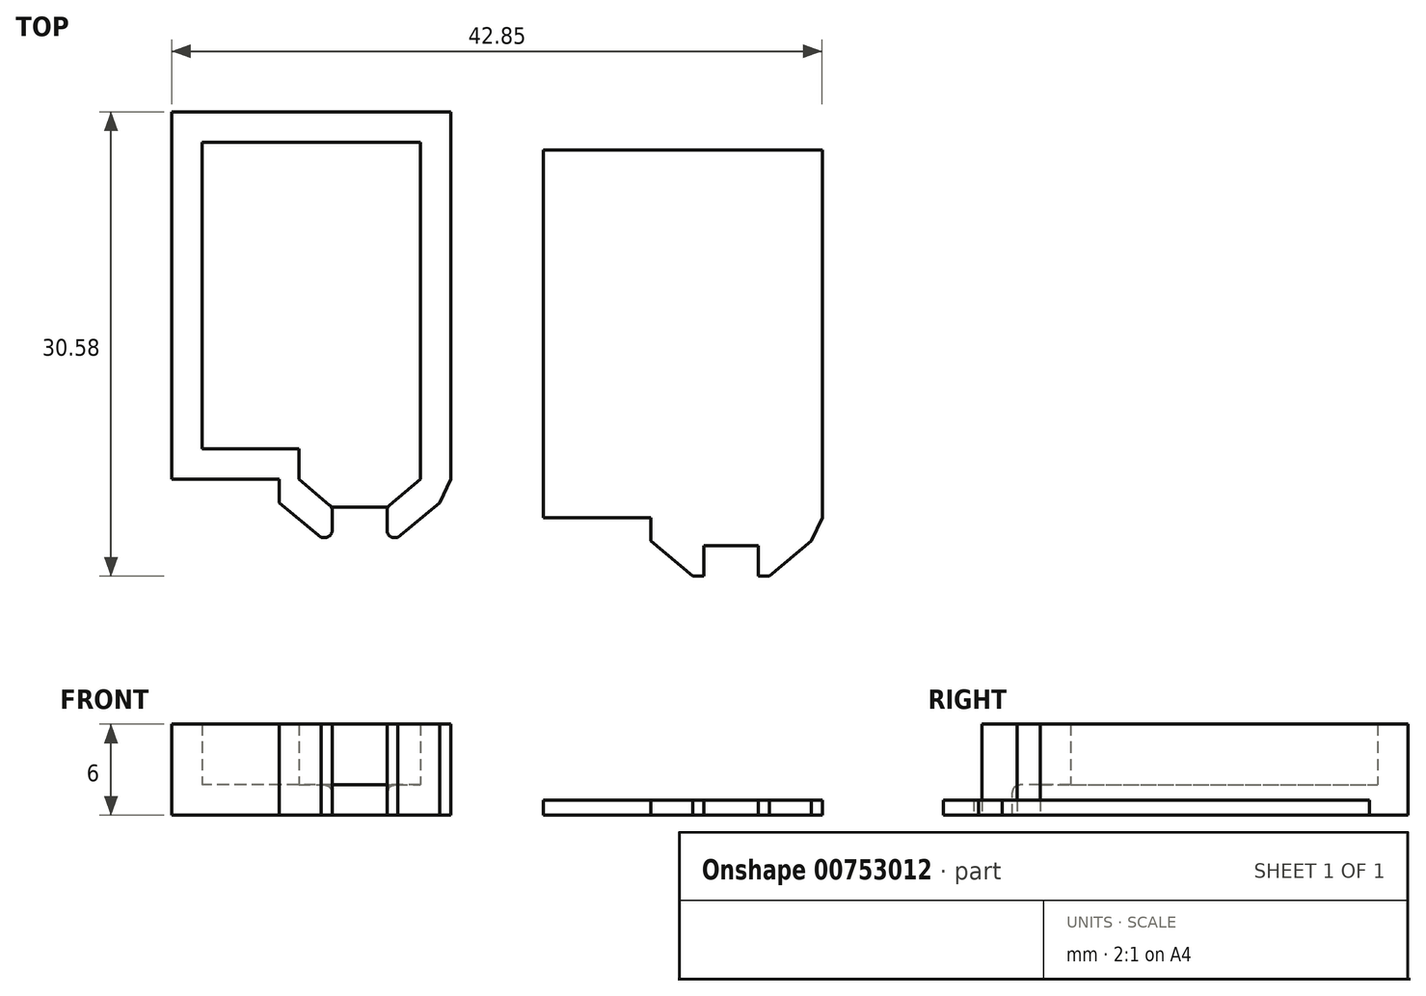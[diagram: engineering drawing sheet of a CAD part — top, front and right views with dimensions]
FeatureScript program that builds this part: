
annotation { "Feature Type Name" : "Feature", "Feature Type Description" : "" }
export const myFeature = defineFeature(function(context is Context, id is Id, definition is map)
    precondition{}
    {
        {
            var Q0;
            Q0=qCreatedBy(makeId("Top.planeOp"),FACE);
            var sketch = newSketch(context, id + "F0", { "sketchPlane" : qUnion([Q0])});
            skLineSegment(sketch, "E0.bottom", {"start": v(7.2, -10.1) * mm, "end": v(-7.19, -10.1) * mm});
            skLineSegment(sketch, "E0.top", {"start": v(7.2, 10.1) * mm, "end": v(-7.19, 10.1) * mm});
            skLineSegment(sketch, "E0.left", {"start": v(7.2, -10.1) * mm, "end": v(7.2, 10.1) * mm});
            skLineSegment(sketch, "E0.right", {"start": v(-7.19, -10.1) * mm, "end": v(-7.19, 10.1) * mm});
            skPoint(sketch, "E0.middle", {"position": v(0, 0) * mm});
            skLineSegment(sketch, "E1.0", {"start": v(9.2, 12.1) * mm, "end": v(-9.19, 12.1) * mm});
            skLineSegment(sketch, "E1.1", {"start": v(9.2, -12.1) * mm, "end": v(9.2, 12.1) * mm});
            skLineSegment(sketch, "E1.2", {"start": v(9.2, -12.1) * mm, "end": v(7.2, -12.1) * mm});
            skLineSegment(sketch, "E1.3", {"start": v(-9.19, -12.1) * mm, "end": v(-9.19, 12.1) * mm});
            skLineSegment(sketch, "E2", {"start": v(7.2, -10.1) * mm, "end": v(7.2, -12.1) * mm});
            skPoint(sketch, "E2.endSnap0", {"position": v(0, -12.1) * mm});
            skLineSegment(sketch, "E3", {"start": v(7.2, -10.1) * mm, "end": v(-0.8, -10.1) * mm, "construction": true});
            skLineSegment(sketch, "E4", {"start": v(-0.8, -10.1) * mm, "end": v(-0.8, -12.1) * mm});
            skLineSegment(sketch, "E5.trimOffspring", {"start": v(-0.8, -12.1) * mm, "end": v(-9.2, -12.1) * mm});
            skLineSegment(sketch, "E6", {"start": v(-0.8, -12.1) * mm, "end": v(7.2, -12.1) * mm});
            skLineSegment(sketch, "E7", {"start": v(-0.8, -12.1) * mm, "end": v(1.4, -13.95) * mm});
            skLineSegment(sketch, "E8", {"start": v(1.4, -13.95) * mm, "end": v(5, -13.95) * mm});
            skLineSegment(sketch, "E9", {"start": v(5, -13.95) * mm, "end": v(7.2, -12.1) * mm});
            skLineSegment(sketch, "E10", {"start": v(-0.8, -12.1) * mm, "end": v(3.2, -12.1) * mm, "construction": true});
            skLineSegment(sketch, "E11", {"start": v(3.2, -12.1) * mm, "end": v(3.2, -19.26) * mm, "construction": true});
            skLineSegment(sketch, "E12.0", {"start": v(5.72, -15.95) * mm, "end": v(8.48, -13.64) * mm});
            skLineSegment(sketch, "E12.1", {"start": v(0.66, -15.95) * mm, "end": v(5.72, -15.95) * mm});
            skLineSegment(sketch, "E12.2", {"start": v(-2.1, -13.64) * mm, "end": v(0.66, -15.95) * mm});
            skLineSegment(sketch, "E13", {"start": v(-2.1, -13.64) * mm, "end": v(-2.1, -12.1) * mm});
            skLineSegment(sketch, "E14", {"start": v(8.48, -13.64) * mm, "end": v(9.2, -12.1) * mm});
            skLineSegment(sketch, "E15", {"start": v(1.4, -13.95) * mm, "end": v(1.4, -15.95) * mm});
            skLineSegment(sketch, "E16", {"start": v(5, -13.95) * mm, "end": v(5, -15.95) * mm});
            skSolve(sketch);
        }
        {
            var Q0;
            Q0=makeQuery(id+"F0.imprint","IMPRINT",FACE,{"disambiguationData":[TD([[makeQuery(id+"F0.imprint","IMPRINT",EDGE,{"derivedFrom":sQuery(id+"F0.wireOp",EDGE,"E0.top")}),1.0]])]});
            extrude(context, id + "F1", {"entities" : qUnion([Q0]), "depth" : 2 * mm, "offsetDistance" : 25 * mm});
        }
        {
            var Q0;
            Q0=makeQuery(id+"F0.imprint","IMPRINT",FACE,{"disambiguationData":[TD([[makeQuery(id+"F0.imprint","IMPRINT",EDGE,{"derivedFrom":sQuery(id+"F0.wireOp",EDGE,"E0.top")}),-1.0]])]});
            extrude(context, id + "F2", {"entities" : qUnion([Q0]), "operationType" : NewBodyOperationType.ADD, "depth" : 5 * mm, "offsetDistance" : 25 * mm});
        }
        {
            var Q0;
            {var subQ0=sQuery(id+"F0.wireOp",EDGE,"E2");Q0=makeQuery(id+"F0.imprint","IMPRINT",FACE,{"disambiguationData":[TD([[makeQuery(id+"F0.imprint","IMPRINT",EDGE,{"derivedFrom":subQ0}),-1.0]])]});}
            extrude(context, id + "F3", {"entities" : qUnion([Q0]), "operationType" : NewBodyOperationType.ADD, "depth" : 2 * mm, "offsetDistance" : 25 * mm});
        }
        {
            var Q0;
            Q0=makeQuery(id+"F0.imprint","IMPRINT",FACE,{"disambiguationData":[TD([[makeQuery(id+"F0.imprint","IMPRINT",EDGE,{"derivedFrom":sQuery(id+"F0.wireOp",EDGE,"E6")}),-1.0]])]});
            extrude(context, id + "F4", {"entities" : qUnion([Q0]), "operationType" : NewBodyOperationType.ADD, "depth" : 2 * mm, "offsetDistance" : 25 * mm});
        }
        {
            var Q0;
            {var subQ3=sQuery(id+"F0.wireOp",EDGE,"E7");Q0=makeQuery(id+"F0.imprint","IMPRINT",FACE,{"disambiguationData":[TD([[makeQuery(id+"F0.imprint","IMPRINT",EDGE,{"derivedFrom":subQ3}),-1.0]])]});}
            var Q1;
            Q1=makeQuery(id+"F0.imprint","IMPRINT",FACE,{"disambiguationData":[TD([[makeQuery(id+"F0.imprint","IMPRINT",EDGE,{"derivedFrom":sQuery(id+"F0.wireOp",EDGE,"E1.2")}),1.0]])]});
            extrude(context, id + "F5", {"entities" : qUnion([Q0, Q1]), "operationType" : NewBodyOperationType.ADD, "depth" : 5 * mm, "offsetDistance" : 25 * mm});
        }
        {
            var Q0;
            Q0=qCreatedBy(makeId("Top.planeOp"),FACE);
            var sketch = newSketch(context, id + "F6", { "sketchPlane" : qUnion([Q0])});
            skLineSegment(sketch, "E17.bottom", {"start": v(31.66, -12.63) * mm, "end": v(17.28, -12.63) * mm});
            skLineSegment(sketch, "E17.top", {"start": v(31.66, 7.58) * mm, "end": v(17.28, 7.58) * mm});
            skLineSegment(sketch, "E17.left", {"start": v(31.66, -12.63) * mm, "end": v(31.66, 7.58) * mm});
            skLineSegment(sketch, "E17.right", {"start": v(17.28, -12.63) * mm, "end": v(17.28, 7.58) * mm});
            skPoint(sketch, "E17.middle", {"position": v(24.47, -2.53) * mm});
            skLineSegment(sketch, "E18.0", {"start": v(33.66, 9.58) * mm, "end": v(15.28, 9.58) * mm});
            skLineSegment(sketch, "E18.1", {"start": v(33.66, -14.63) * mm, "end": v(33.66, 9.58) * mm});
            skLineSegment(sketch, "E18.2", {"start": v(33.66, -14.63) * mm, "end": v(31.66, -14.63) * mm});
            skLineSegment(sketch, "E18.3", {"start": v(15.28, -14.63) * mm, "end": v(15.28, 9.58) * mm});
            skLineSegment(sketch, "E19", {"start": v(31.66, -12.63) * mm, "end": v(31.66, -14.63) * mm});
            skPoint(sketch, "E19.endSnap0", {"position": v(24.47, -14.63) * mm});
            skLineSegment(sketch, "E20", {"start": v(31.66, -12.63) * mm, "end": v(23.66, -12.63) * mm, "construction": true});
            skLineSegment(sketch, "E21", {"start": v(23.66, -12.63) * mm, "end": v(23.66, -14.63) * mm});
            skLineSegment(sketch, "E22.trimOffspring", {"start": v(23.66, -14.63) * mm, "end": v(15.28, -14.63) * mm});
            skLineSegment(sketch, "E23", {"start": v(23.66, -14.63) * mm, "end": v(31.66, -14.63) * mm});
            skLineSegment(sketch, "E24", {"start": v(23.66, -14.63) * mm, "end": v(25.86, -16.48) * mm});
            skLineSegment(sketch, "E25", {"start": v(25.86, -16.48) * mm, "end": v(29.46, -16.48) * mm});
            skLineSegment(sketch, "E26", {"start": v(29.46, -16.48) * mm, "end": v(31.66, -14.63) * mm});
            skLineSegment(sketch, "E27", {"start": v(23.66, -14.63) * mm, "end": v(27.66, -14.63) * mm, "construction": true});
            skLineSegment(sketch, "E28", {"start": v(27.66, -14.63) * mm, "end": v(27.66, -21.79) * mm, "construction": true});
            skLineSegment(sketch, "E29.0", {"start": v(30.2, -18.48) * mm, "end": v(32.95, -16.17) * mm});
            skLineSegment(sketch, "E29.1", {"start": v(25.13, -18.48) * mm, "end": v(30.2, -18.48) * mm});
            skLineSegment(sketch, "E29.2", {"start": v(22.38, -16.17) * mm, "end": v(25.13, -18.48) * mm});
            skLineSegment(sketch, "E30", {"start": v(22.38, -16.17) * mm, "end": v(22.38, -14.63) * mm});
            skLineSegment(sketch, "E31", {"start": v(32.95, -16.17) * mm, "end": v(33.66, -14.63) * mm});
            skLineSegment(sketch, "E32", {"start": v(25.86, -16.48) * mm, "end": v(25.86, -18.48) * mm});
            skLineSegment(sketch, "E33", {"start": v(29.46, -16.48) * mm, "end": v(29.46, -18.48) * mm});
            skSolve(sketch);
        }
        {
            var Q0;
            Q0=makeQuery(id+"F6.imprint","IMPRINT",FACE,{"disambiguationData":[TD([[makeQuery(id+"F6.imprint","IMPRINT",EDGE,{"derivedFrom":sQuery(id+"F6.wireOp",EDGE,"E17.top")}),1.0]])]});
            var Q1;
            Q1=makeQuery(id+"F6.imprint","IMPRINT",FACE,{"disambiguationData":[TD([[makeQuery(id+"F6.imprint","IMPRINT",EDGE,{"derivedFrom":sQuery(id+"F6.wireOp",EDGE,"E17.top")}),-1.0]])]});
            var Q2;
            {var subQ0=sQuery(id+"F6.wireOp",EDGE,"E19");Q2=makeQuery(id+"F6.imprint","IMPRINT",FACE,{"disambiguationData":[TD([[makeQuery(id+"F6.imprint","IMPRINT",EDGE,{"derivedFrom":subQ0}),-1.0]])]});}
            var Q3;
            Q3=makeQuery(id+"F6.imprint","IMPRINT",FACE,{"disambiguationData":[TD([[makeQuery(id+"F6.imprint","IMPRINT",EDGE,{"derivedFrom":sQuery(id+"F6.wireOp",EDGE,"E23")}),-1.0]])]});
            var Q4;
            {var subQ3=sQuery(id+"F6.wireOp",EDGE,"E24");Q4=makeQuery(id+"F6.imprint","IMPRINT",FACE,{"disambiguationData":[TD([[makeQuery(id+"F6.imprint","IMPRINT",EDGE,{"derivedFrom":subQ3}),-1.0]])]});}
            var Q5;
            Q5=makeQuery(id+"F6.imprint","IMPRINT",FACE,{"disambiguationData":[TD([[makeQuery(id+"F6.imprint","IMPRINT",EDGE,{"derivedFrom":sQuery(id+"F6.wireOp",EDGE,"E18.2")}),1.0]])]});
            extrude(context, id + "F7", {"entities" : qUnion([Q0, Q1, Q2, Q3, Q4, Q5]), "depth" : 1 * mm, "offsetDistance" : 25 * mm});
        }
        {
            var Q0;
            {var subQ0=sQuery(id+"F0.wireOp",EDGE,"E12.1");var subQ1=sQuery(id+"F0.wireOp",EDGE,"E5.trimOffspring");var subQ2=sQuery(id+"F0.wireOp",EDGE,"E1.2");Q0=makeQuery(id+"F5.boolean.opBoolean","MERGE",FACE,{"derivedFrom":[makeQuery(id+"F2.opExtrude","CAP_FACE",FACE,{"disambiguationData":[OSD([sQuery(id+"F0.wireOp",EDGE,"E0.bottom"),sQuery(id+"F0.wireOp",EDGE,"E0.top"),sQuery(id+"F0.wireOp",EDGE,"E0.left"),sQuery(id+"F0.wireOp",EDGE,"E0.right"),sQuery(id+"F0.wireOp",EDGE,"E1.0"),sQuery(id+"F0.wireOp",EDGE,"E1.1"),subQ2,sQuery(id+"F0.wireOp",EDGE,"E1.3"),sQuery(id+"F0.wireOp",EDGE,"E2"),sQuery(id+"F0.wireOp",EDGE,"E4"),subQ1])],"isStart":false}),makeQuery(id+"F5.opExtrude","CAP_FACE",FACE,{"disambiguationData":[OSD([subQ2,sQuery(id+"F0.wireOp",EDGE,"E9"),sQuery(id+"F0.wireOp",EDGE,"E12.0"),subQ0,sQuery(id+"F0.wireOp",EDGE,"E14"),sQuery(id+"F0.wireOp",EDGE,"E16")])],"isStart":false}),makeQuery(id+"F5.opExtrude","CAP_FACE",FACE,{"disambiguationData":[OSD([subQ1,sQuery(id+"F0.wireOp",EDGE,"E7"),subQ0,sQuery(id+"F0.wireOp",EDGE,"E12.2"),sQuery(id+"F0.wireOp",EDGE,"E13"),sQuery(id+"F0.wireOp",EDGE,"E15")])],"isStart":false})]});}
            extrude(context, id + "F8", {"entities" : qUnion([Q0]), "operationType" : NewBodyOperationType.ADD, "depth" : 1 * mm, "offsetDistance" : 25 * mm});
        }
        {
            var Q0;
            {var subQ0=sQuery(id+"F0.wireOp",EDGE,"E15");var subQ1=sQuery(id+"F0.wireOp",EDGE,"E12.1");Q0=makeQuery(id+"F8.boolean.opBoolean","MERGE",EDGE,{"derivedFrom":[makeQuery(id+"F5.opExtrude","SWEPT_EDGE",EDGE,{"disambiguationData":[OSD([subQ1,subQ0])]}),makeQuery(id+"F8.opExtrude","SWEPT_EDGE",EDGE,{"disambiguationData":[OSD([subQ1,subQ0])]})]});}
            var Q1;
            {var subQ0=sQuery(id+"F0.wireOp",EDGE,"E16");var subQ1=sQuery(id+"F0.wireOp",EDGE,"E9");var subQ2=sQuery(id+"F0.wireOp",EDGE,"E8");Q1=makeQuery(id+"F8.boolean.opBoolean","MERGE",EDGE,{"derivedFrom":[makeQuery(id+"F5.boolean.opBoolean","SPLIT",EDGE,{"derivedFrom":makeQuery(id+"F5.opExtrude","SWEPT_EDGE",EDGE,{"disambiguationData":[OSD([subQ2,subQ1,subQ0])]})}),makeQuery(id+"F8.opExtrude","SWEPT_EDGE",EDGE,{"disambiguationData":[OSD([subQ2,subQ1,subQ0])]})]});}
            var Q2;
            {var subQ0=sQuery(id+"F0.wireOp",EDGE,"E16");var subQ1=sQuery(id+"F0.wireOp",EDGE,"E12.1");Q2=makeQuery(id+"F8.boolean.opBoolean","MERGE",EDGE,{"derivedFrom":[makeQuery(id+"F5.opExtrude","SWEPT_EDGE",EDGE,{"disambiguationData":[OSD([subQ1,subQ0])]}),makeQuery(id+"F8.opExtrude","SWEPT_EDGE",EDGE,{"disambiguationData":[OSD([subQ1,subQ0])]})]});}
            var Q3;
            Q3=makeQuery(id+"F4.opExtrude","CAP_EDGE",EDGE,{"disambiguationData":[OSD([sQuery(id+"F0.wireOp",EDGE,"E8")])],"isStart":false});
            var Q4;
            {var subQ0=sQuery(id+"F0.wireOp",EDGE,"E15");var subQ1=sQuery(id+"F0.wireOp",EDGE,"E8");var subQ2=sQuery(id+"F0.wireOp",EDGE,"E7");Q4=makeQuery(id+"F8.boolean.opBoolean","MERGE",EDGE,{"derivedFrom":[makeQuery(id+"F5.boolean.opBoolean","SPLIT",EDGE,{"derivedFrom":makeQuery(id+"F5.opExtrude","SWEPT_EDGE",EDGE,{"disambiguationData":[OSD([subQ2,subQ1,subQ0])]})}),makeQuery(id+"F8.opExtrude","SWEPT_EDGE",EDGE,{"disambiguationData":[OSD([subQ2,subQ1,subQ0])]})]});}
            fillet(context, id + "F9", {"entities" : qUnion([Q0, Q1, Q2, Q3, Q4]), "radius" : 0.5 * mm, "tangentPropagation" : true, "allowEdgeOverflow" : false});
        }
    });
